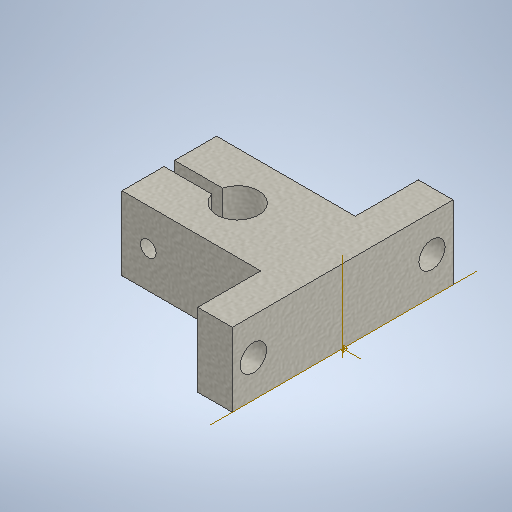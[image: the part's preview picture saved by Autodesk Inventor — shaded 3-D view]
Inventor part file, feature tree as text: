
AUTODESK INVENTOR PART (.ipt)
format: ipt  version: 2025.2 (Build 292293000, 293)  size: 326,656 bytes
history: native  units: mm
features: extrude x3, sketch x3
ambient origin geometry x8: Origin, YZ Plane, XZ Plane, XY Plane, X Axis, Y Axis, Z Axis, Center Point
bodies: Solid1 (feature_tree)
feature tree (6):
  extrude  "Extrusion1"  Depth=21.0mm
  extrude  "Extrusion2"  Depth=9.0mm
  extrude  "Extrusion3"  Depth=33.0mm
  sketch  "Sketch1"  dims[d0=6.6mm d1=21.0mm]
  sketch  "Sketch2"  dims[d2=1.0mm d3=9.0mm]
  sketch  "Sketch3"  dims[d4=8.0mm d5=33.0mm d8=14.0mm d9=0.0mm d10=5.0mm d12=14.0mm d13=0.0mm d14=4.0mm d15=3.0mm d16=5.0mm d17=3.0mm d18=0.0mm d19=20.0mm]
